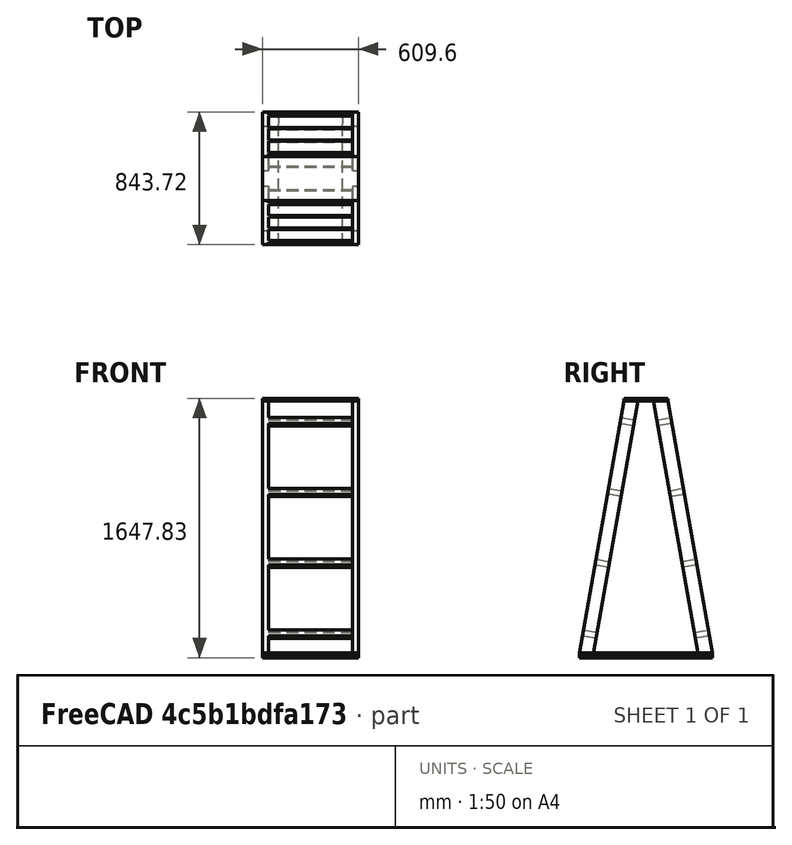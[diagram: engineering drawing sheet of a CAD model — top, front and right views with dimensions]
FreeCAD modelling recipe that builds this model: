
FCSTD DOCUMENT  (FreeCAD 0.20R29410 (Git))
Label: ClampRack
License: All rights reserved
LicenseURL: http://en.wikipedia.org/wiki/All_rights_reserved
objects: TechDraw::DrawViewDimension×22, Sketcher::SketchObject×13, PartDesign::Pad×12, Part::Part2DObjectPython×10, PartDesign::Body×10, TechDraw::DrawViewPart×6, TechDraw::DrawProjGroupItem×6, TechDraw::DrawSVGTemplate×3, TechDraw::DrawProjGroup×3, TechDraw::DrawPage×3, PartDesign::Plane×2, Spreadsheet::Sheet×1, App::LinkGroup×1
note: 59 computed .brp shape members not serialized (recipe doc carries the construction recipe); baked Part::Feature solids carry a one-line shape summary decoded from their .brp

FEATURE [Sketcher::SketchObject] Sketch  label="YZ_profile"
  FullyConstrained = true
  MapMode = 5
  Placement = pos=(0,0,0) rot=(0.57735,0.57735,0.57735;2.0944rad)
  Support = -> [YZ_Plane]
  expr: Constraints[14] = <<Spreadsheet>>.riser_z
  expr: Constraints[23] = <<Spreadsheet>>.shelf_stock_height
  expr: Constraints[35] = <<Spreadsheet>>.top_shelf_y
  expr: Constraints[50] = <<Spreadsheet>>.shelf_stock_height
  expr: Constraints[77] = <<Spreadsheet>>.riser_stock_width
  expr: Constraints[9] = <<Spreadsheet>>.shelf_stock_height
  sketch-geometry (29):
    g0: LineSegment StartX=-421.858 StartY=0 StartZ=0 EndX=421.858 EndY=0 EndZ=0
    g1: LineSegment StartX=421.858 StartY=0 StartZ=0 EndX=421.858 EndY=-15.875 EndZ=0
    g2: LineSegment StartX=421.858 StartY=-15.875 StartZ=0 EndX=-421.858 EndY=-15.875 EndZ=0
    g3: LineSegment StartX=-421.858 StartY=-15.875 StartZ=0 EndX=-421.858 EndY=0 EndZ=0
    g4: LineSegment StartX=-331.587 StartY=0 StartZ=0 EndX=-49.4286 EndY=1600.2 EndZ=0
    g5: LineSegment StartX=-49.4286 StartY=1600.2 StartZ=0 EndX=-139.7 EndY=1600.2 EndZ=0
    g6: LineSegment StartX=-139.7 StartY=1600.2 StartZ=0 EndX=139.7 EndY=1600.2 EndZ=0
    g7: LineSegment StartX=139.7 StartY=1600.2 StartZ=0 EndX=139.7 EndY=1616.08 EndZ=0
    g8: LineSegment StartX=139.7 StartY=1616.08 StartZ=0 EndX=-139.7 EndY=1616.08 EndZ=0
    g9: LineSegment StartX=-139.7 StartY=1616.08 StartZ=0 EndX=-139.7 EndY=1600.2 EndZ=0
    g10: LineSegment StartX=139.7 StartY=1600.2 StartZ=0 EndX=49.4286 EndY=1600.2 EndZ=0
    g11: LineSegment StartX=49.4286 StartY=1600.2 StartZ=0 EndX=331.587 EndY=0 EndZ=0
    g12: LineSegment StartX=331.587 StartY=0 StartZ=0 EndX=421.858 EndY=0 EndZ=0
    g13: LineSegment StartX=-139.7 StartY=1600.2 StartZ=0 EndX=-161.753 EndY=1475.13 EndZ=0
    g14: LineSegment StartX=-399.805 StartY=125.071 StartZ=0 EndX=-421.858 EndY=0 EndZ=0
    g15: LineSegment StartX=-421.858 StartY=-15.875 StartZ=0 EndX=421.858 EndY=-15.875 EndZ=0
    g16: LineSegment StartX=421.858 StartY=-15.875 StartZ=0 EndX=421.858 EndY=-31.75 EndZ=0
    g17: LineSegment StartX=421.858 StartY=-31.75 StartZ=0 EndX=-421.858 EndY=-31.75 EndZ=0
    g18: LineSegment StartX=-421.858 StartY=-31.75 StartZ=0 EndX=-421.858 EndY=-15.875 EndZ=0
    g19: LineSegment StartX=-161.753 StartY=1475.13 StartZ=0 EndX=-241.104 EndY=1025.11 EndZ=0
    g20: LineSegment StartX=-241.104 StartY=1025.11 StartZ=0 EndX=-320.455 EndY=575.09 EndZ=0
    g21: LineSegment StartX=-320.455 StartY=575.09 StartZ=0 EndX=-399.805 EndY=125.071 EndZ=0
    g22: LineSegment StartX=161.753 StartY=1475.13 StartZ=0 EndX=139.7 EndY=1600.2 EndZ=0
    g23: LineSegment StartX=421.858 StartY=0 StartZ=0 EndX=399.805 EndY=125.071 EndZ=0
    g24: LineSegment StartX=241.104 StartY=1025.11 StartZ=0 EndX=161.753 EndY=1475.13 EndZ=0
    g25: LineSegment StartX=399.805 StartY=125.071 StartZ=0 EndX=320.455 EndY=575.09 EndZ=0
    g26: LineSegment StartX=320.455 StartY=575.09 StartZ=0 EndX=241.104 EndY=1025.11 EndZ=0
    g27: LineSegment StartX=-161.753 StartY=1475.13 StartZ=0 EndX=-74.2039 EndY=1459.69 EndZ=0
    g28: LineSegment StartX=161.753 StartY=1475.13 StartZ=0 EndX=74.2039 EndY=1459.69 EndZ=0
  constraints (78):
    c: Coincident(g0,g1)
    c: Coincident(g1,g2)
    c: Coincident(g2,g3)
    c: Coincident(g3,g0)
    c: Horizontal(g0)
    c: Horizontal(g2)
    c: Vertical(g1)
    c: Vertical(g3)
    c: Symmetric(g0,g0,g-1)
    c: DistanceY(g3,g3) = 15.875
    c: PointOnObject(g4,g0)
    c: Horizontal(g5)
    c: Coincident(g5,g13)
    c: Coincident(g14,g0)
    c: DistanceY(g4,g4) = 1600.2
    c: Angle(g4,g-2) = 0.174533
    c: Coincident(g6,g7)
    c: Coincident(g7,g8)
    c: Coincident(g8,g9)
    c: Coincident(g9,g6)
    c: Horizontal(g6)
    c: Vertical(g7)
    c: Vertical(g9)
    c: DistanceY(g6,g8) = 15.875
    c: Coincident(g6,g5)
    c: Symmetric(g8,g7,g-2)
    c: Coincident(g5,g4)
    c: Coincident(g0,g23)
    c: Coincident(g22,g6)
    c: Coincident(g22,g10)
    c: PointOnObject(g10,g6)
    c: Coincident(g10,g11)
    c: PointOnObject(g11,g0)
    c: Coincident(g11,g12)
    c: Coincident(g12,g23)
    c: DistanceX(g8,g8) = 279.4
    c: Coincident(g13,g19)
    c: Parallel(g4,g13)
    c: Coincident(g21,g14)
    c: Parallel(g4,g14)
    c: Distance(g13) = 127
    c: Coincident(g15,g16)
    c: Coincident(g16,g17)
    c: Coincident(g17,g18)
    c: Coincident(g18,g15)
    c: Horizontal(g17)
    c: Vertical(g16)
    c: Vertical(g18)
    c: Coincident(g15,g2)
    c: Coincident(g1,g15)
    c: DistanceY(g18,g18) = 15.875
    c: Coincident(g19,g20)
    c: Parallel(g4,g19)
    c: Coincident(g20,g21)
    c: Parallel(g4,g20)
    c: Parallel(g4,g21)
    c: Equal(g21,g20)
    c: Equal(g20,g19)
    c: Coincident(g24,g22)
    c: Parallel(g11,g22)
    c: Coincident(g23,g25)
    c: Coincident(g26,g24)
    c: Parallel(g11,g24)
    c: Coincident(g25,g26)
    c: Parallel(g11,g25)
    c: Equal(g25,g26)
    c: Equal(g26,g24)
    c: Coincident(g27,g13)
    c: PointOnObject(g27,g4)
    c: Coincident(g28,g22)
    c: PointOnObject(g28,g11)
    c: Perpendicular(g27,g13)
    c: Perpendicular(g28,g22)
    c: Symmetric(g13,g22,g-2)
    c: Symmetric(g14,g23,g-2)
    c: Distance(g14,g0) = 127
    c: Distance(g27) = 88.9
    c: Distance(g28) = 88.9
FEATURE [Part::Part2DObjectPython] Clone2D  label="YZ_profile (2D)"  # Draft 2D object (typed FeaturePython)
  Fuse = false
  Objects = -> [Sketch]
  Placement = pos=(0,0,0) rot=(0.57735,0.57735,0.57735;2.0944rad)
  Scale = (1,1,1)
FEATURE [Sketcher::SketchObject] Sketch001
  ExternalGeometry = -> [Clone2D]
  FullyConstrained = true
  MapMode = 5
  Placement = pos=(0,0,0) rot=(0.57735,0.57735,0.57735;2.0944rad)
  Support = -> [YZ_Plane]
  sketch-geometry (4):
    g0: LineSegment StartX=-421.858 StartY=-2.13e-14 StartZ=0 EndX=421.858 EndY=-2.13e-14 EndZ=0
    g1: LineSegment StartX=421.858 StartY=-2.13e-14 StartZ=0 EndX=421.858 EndY=-15.875 EndZ=0
    g2: LineSegment StartX=421.858 StartY=-15.875 StartZ=0 EndX=-421.858 EndY=-15.875 EndZ=0
    g3: LineSegment StartX=-421.858 StartY=-15.875 StartZ=0 EndX=-421.858 EndY=-2.13e-14 EndZ=0
  constraints (9):
    c: Coincident(g0,g1)
    c: Coincident(g1,g2)
    c: Coincident(g2,g3)
    c: Coincident(g3,g0)
    c: Horizontal(g2)
    c: Vertical(g1)
    c: Coincident(g0,g-4)
    c: Coincident(g-5,g2)
    c: Coincident(g0,g-6)
FEATURE [PartDesign::Pad] Pad
  Direction = (1,-2e-16,3e-16)
  Length = 609.6
  Length2 = 10
  Midplane = true
  Placement = pos=(0,0,0) rot=(0.57735,0.57735,0.57735;2.0944rad)
  Profile = -> Sketch001
  ReferenceAxis = -> Sketch001 [N_Axis]
  Refine = true
  Type = 0
  expr: Length = Spreadsheet.width_x
FEATURE [PartDesign::Body] Body  label="BottomShelf"
  Group = -> [Clone2D,Sketch001,Pad]
  Origin = -> Origin
  Tip = -> Pad
FEATURE [Part::Part2DObjectPython] Clone2D001  label="YZ_profile (2D)001"  # Draft 2D object (typed FeaturePython)
  Fuse = false
  Objects = -> [Sketch]
  Placement = pos=(0,0,0) rot=(0.57735,0.57735,0.57735;2.0944rad)
  Scale = (1,1,1)
FEATURE [Sketcher::SketchObject] Sketch005
  ExternalGeometry = -> [Clone2D001]
  FullyConstrained = true
  MapMode = 5
  Placement = pos=(0,0,0) rot=(0.57735,0.57735,0.57735;2.0944rad)
  Support = -> [YZ_Plane004]
  sketch-geometry (4):
    g0: LineSegment StartX=-421.858 StartY=-2.84e-14 StartZ=0 EndX=-139.7 EndY=1600.2 EndZ=0
    g1: LineSegment StartX=-139.7 StartY=1600.2 StartZ=0 EndX=-49.4286 EndY=1600.2 EndZ=0
    g2: LineSegment StartX=-49.4286 StartY=1600.2 StartZ=0 EndX=-331.587 EndY=0 EndZ=0
    g3: LineSegment StartX=-331.587 StartY=0 StartZ=0 EndX=-421.858 EndY=-2.84e-14 EndZ=0
  constraints (8):
    c: Coincident(g0,g1)
    c: Coincident(g1,g2)
    c: Coincident(g2,g3)
    c: Coincident(g3,g0)
    c: Coincident(g0,g-3)
    c: Coincident(g1,g-4)
    c: Coincident(g0,g-5)
    c: Coincident(g2,g-6)
FEATURE [PartDesign::Pad] Pad003
  Direction = (1,-2e-16,3e-16)
  Length = 38.1
  Length2 = 10
  Midplane = true
  Placement = pos=(0,0,0) rot=(0.57735,0.57735,0.57735;2.0944rad)
  Profile = -> Sketch005
  ReferenceAxis = -> Sketch005 [N_Axis]
  Refine = true
  Type = 0
FEATURE [PartDesign::Body] Body003  label="RiserFtRt"
  Group = -> [Clone2D001,Sketch005,Pad003]
  Origin = -> Origin003
  Placement = pos=(285.75,0,0) rot=(0,0,1;0rad)
  Tip = -> Pad003
FEATURE [Part::Part2DObjectPython] Clone2D002  label="YZ_profile (2D)002"  # Draft 2D object (typed FeaturePython)
  Fuse = false
  Objects = -> [Sketch]
  Placement = pos=(0,0,0) rot=(0.57735,0.57735,0.57735;2.0944rad)
  Scale = (1,1,1)
FEATURE [Sketcher::SketchObject] Sketch006
  ExternalGeometry = -> [Clone2D002]
  FullyConstrained = true
  MapMode = 5
  Placement = pos=(0,0,0) rot=(0.57735,0.57735,0.57735;2.0944rad)
  Support = -> [YZ_Plane004]
  sketch-geometry (4):
    g0: LineSegment StartX=-421.858 StartY=-2.84e-14 StartZ=0 EndX=-139.7 EndY=1600.2 EndZ=0
    g1: LineSegment StartX=-139.7 StartY=1600.2 StartZ=0 EndX=-49.4286 EndY=1600.2 EndZ=0
    g2: LineSegment StartX=-49.4286 StartY=1600.2 StartZ=0 EndX=-331.587 EndY=0 EndZ=0
    g3: LineSegment StartX=-331.587 StartY=0 StartZ=0 EndX=-421.858 EndY=-2.84e-14 EndZ=0
  constraints (8):
    c: Coincident(g0,g1)
    c: Coincident(g1,g2)
    c: Coincident(g2,g3)
    c: Coincident(g3,g0)
    c: Coincident(g0,g-3)
    c: Coincident(g1,g-4)
    c: Coincident(g0,g-5)
    c: Coincident(g2,g-6)
FEATURE [PartDesign::Pad] Pad004
  Direction = (1,-2e-16,3e-16)
  Length = 38.1
  Length2 = 10
  Midplane = true
  Placement = pos=(0,0,0) rot=(0.57735,0.57735,0.57735;2.0944rad)
  Profile = -> Sketch006
  ReferenceAxis = -> Sketch006 [N_Axis]
  Refine = true
  Type = 0
FEATURE [Part::Part2DObjectPython] Clone2D003  label="YZ_profile (2D)003"  # Draft 2D object (typed FeaturePython)
  Fuse = false
  Objects = -> [Sketch]
  Placement = pos=(0,0,0) rot=(0.57735,0.57735,0.57735;2.0944rad)
  Scale = (1,1,1)
FEATURE [Sketcher::SketchObject] Sketch007
  ExternalGeometry = -> [Clone2D003]
  FullyConstrained = true
  MapMode = 5
  Placement = pos=(0,0,0) rot=(0.57735,0.57735,0.57735;2.0944rad)
  Support = -> [YZ_Plane005]
  sketch-geometry (4):
    g0: LineSegment StartX=49.4286 StartY=1600.2 StartZ=0 EndX=139.7 EndY=1600.2 EndZ=0
    g1: LineSegment StartX=139.7 StartY=1600.2 StartZ=0 EndX=421.858 EndY=0 EndZ=0
    g2: LineSegment StartX=421.858 StartY=0 StartZ=0 EndX=331.587 EndY=2.13e-14 EndZ=0
    g3: LineSegment StartX=331.587 StartY=2.13e-14 StartZ=0 EndX=49.4286 EndY=1600.2 EndZ=0
  constraints (8):
    c: Coincident(g0,g1)
    c: Coincident(g1,g2)
    c: Coincident(g2,g3)
    c: Coincident(g3,g0)
    c: Coincident(g0,g-4)
    c: Coincident(g1,g-6)
    c: Coincident(g2,g-5)
    c: Coincident(g-3,g0)
FEATURE [PartDesign::Pad] Pad005
  Direction = (1,-2e-16,3e-16)
  Length = 38.1
  Length2 = 10
  Placement = pos=(0,0,0) rot=(0.57735,0.57735,0.57735;2.0944rad)
  Profile = -> Sketch007
  ReferenceAxis = -> Sketch007 [N_Axis]
  Refine = true
  Type = 0
FEATURE [PartDesign::Body] Body005  label="RiserRrRt"
  Group = -> [Clone2D003,Sketch007,Pad005]
  Origin = -> Origin005
  Placement = pos=(266.7,0,0) rot=(0,0,1;0rad)
  Tip = -> Pad005
FEATURE [Part::Part2DObjectPython] Clone2D004  label="YZ_profile (2D)004"  # Draft 2D object (typed FeaturePython)
  Fuse = false
  Objects = -> [Sketch]
  Placement = pos=(0,0,0) rot=(0.57735,0.57735,0.57735;2.0944rad)
  Scale = (1,1,1)
FEATURE [Sketcher::SketchObject] Sketch008
  ExternalGeometry = -> [Clone2D004]
  FullyConstrained = true
  MapMode = 5
  Placement = pos=(0,0,0) rot=(0.57735,0.57735,0.57735;2.0944rad)
  Support = -> [YZ_Plane005]
  sketch-geometry (4):
    g0: LineSegment StartX=49.4286 StartY=1600.2 StartZ=0 EndX=139.7 EndY=1600.2 EndZ=0
    g1: LineSegment StartX=139.7 StartY=1600.2 StartZ=0 EndX=421.858 EndY=0 EndZ=0
    g2: LineSegment StartX=421.858 StartY=0 StartZ=0 EndX=331.587 EndY=2.13e-14 EndZ=0
    g3: LineSegment StartX=331.587 StartY=2.13e-14 StartZ=0 EndX=49.4286 EndY=1600.2 EndZ=0
  constraints (8):
    c: Coincident(g0,g1)
    c: Coincident(g1,g2)
    c: Coincident(g2,g3)
    c: Coincident(g3,g0)
    c: Coincident(g0,g-4)
    c: Coincident(g1,g-6)
    c: Coincident(g2,g-5)
    c: Coincident(g-3,g0)
FEATURE [PartDesign::Pad] Pad006
  Direction = (1,-2e-16,3e-16)
  Length = 38.1
  Length2 = 10
  Placement = pos=(0,0,0) rot=(0.57735,0.57735,0.57735;2.0944rad)
  Profile = -> Sketch008
  ReferenceAxis = -> Sketch008 [N_Axis]
  Refine = true
  Type = 0
FEATURE [Part::Part2DObjectPython] Clone2D005  label="YZ_profile (2D)005"  # Draft 2D object (typed FeaturePython)
  Fuse = false
  Objects = -> [Sketch]
  Placement = pos=(0,0,0) rot=(0.57735,0.57735,0.57735;2.0944rad)
  Scale = (1,1,1)
FEATURE [Sketcher::SketchObject] Sketch009
  ExternalGeometry = -> [Clone2D005]
  FullyConstrained = true
  MapMode = 5
  Placement = pos=(0,0,0) rot=(0.57735,0.57735,0.57735;2.0944rad)
  Support = -> [YZ_Plane006]
  sketch-geometry (4):
    g0: LineSegment StartX=-139.7 StartY=1616.08 StartZ=0 EndX=139.7 EndY=1616.08 EndZ=0
    g1: LineSegment StartX=139.7 StartY=1616.08 StartZ=0 EndX=139.7 EndY=1600.2 EndZ=0
    g2: LineSegment StartX=139.7 StartY=1600.2 StartZ=0 EndX=-139.7 EndY=1600.2 EndZ=0
    g3: LineSegment StartX=-139.7 StartY=1600.2 StartZ=0 EndX=-139.7 EndY=1616.08 EndZ=0
  constraints (8):
    c: Coincident(g0,g1)
    c: Coincident(g1,g2)
    c: Coincident(g2,g3)
    c: Coincident(g3,g0)
    c: Coincident(g0,g-3)
    c: Coincident(g2,g-4)
    c: Coincident(g1,g-5)
    c: Coincident(g0,g-6)
FEATURE [PartDesign::Pad] Pad007
  Direction = (1,-2e-16,3e-16)
  Length = 609.6
  Length2 = 10
  Midplane = true
  Placement = pos=(0,0,0) rot=(0.57735,0.57735,0.57735;2.0944rad)
  Profile = -> Sketch009
  ReferenceAxis = -> Sketch009 [N_Axis]
  Refine = true
  Type = 0
  expr: Length = Spreadsheet.width_x
FEATURE [PartDesign::Body] Body007  label="TopShelf"
  Group = -> [Clone2D005,Sketch009,Pad007]
  Origin = -> Origin007
  Tip = -> Pad007
FEATURE [Spreadsheet::Sheet] Spreadsheet
  cells = A2=riser_stock_width; B2(riser_stock_width)==3.5"; C2==3.5"; A3=riser_stock_height; B3(riser_stock_height)==1.5"; C3==1.5"; A4=stretcher_stock_width; B4(stretcher_stock_width)==3.5"; C4==3.5"; A5=stretcher_stock_height; B5(stretcher_stock_height)==1.5"; C5==1.5"; A6=shelf_stock_height; B6(shelf_stock_height)==1" * 5 / 8; C6==1" * 5 / 8; A7=width; B7(width_x)==24"; C7==24"; A8=riser_z; B8(riser_z)==5' + 3"; C8==5' + 3"; A9=top_shelf_y; B9(top_shelf_y)==11"; C9==11"; A10=stretcher_x; B10(stretcher_x)==width_x - 2 * riser_stock_height; C10==width_x - 2 * riser_stock_height; A11=base_rail_width; B11(base_rail_width)==4"; C11==4"; A12=base_stock_height; B12(base_stock_height)==1" * 5 / 8; C12==1" * 5 / 8
FEATURE [PartDesign::Plane] DatumPlane
  Length = 60
  MapMode = 5
  Placement = pos=(19.05,-8.5e-15,6.3e-15) rot=(0.57735,0.57735,0.57735;2.0944rad)
  ResizeMode = 0
  Support = -> [Pad004]
  Width = 60
FEATURE [Sketcher::SketchObject] Sketch010
  ExternalGeometry = -> [Clone2D002]
  FullyConstrained = true
  MapMode = 5
  Placement = pos=(19.05,-8.5e-15,6.3e-15) rot=(0.57735,0.57735,0.57735;2.0944rad)
  Support = -> [DatumPlane]
  expr: Constraints[35] = <<Spreadsheet>>.stretcher_stock_width
  expr: Constraints[36] = <<Spreadsheet>>.stretcher_stock_height
  sketch-geometry (16):
    g0: LineSegment StartX=-237.796 StartY=1043.87 StartZ=0 EndX=-150.247 EndY=1028.43 EndZ=0
    g1: LineSegment StartX=-150.247 StartY=1028.43 StartZ=0 EndX=-156.863 EndY=990.912 EndZ=0
    g2: LineSegment StartX=-156.863 StartY=990.912 StartZ=0 EndX=-244.412 EndY=1006.35 EndZ=0
    g3: LineSegment StartX=-244.412 StartY=1006.35 StartZ=0 EndX=-237.796 EndY=1043.87 EndZ=0
    g4: LineSegment StartX=-317.147 StartY=593.851 StartZ=0 EndX=-229.597 EndY=578.413 EndZ=0
    g5: LineSegment StartX=-229.597 StartY=578.413 StartZ=0 EndX=-236.213 EndY=540.892 EndZ=0
    g6: LineSegment StartX=-236.213 StartY=540.892 StartZ=0 EndX=-323.763 EndY=556.33 EndZ=0
    g7: LineSegment StartX=-323.763 StartY=556.33 StartZ=0 EndX=-317.147 EndY=593.851 EndZ=0
    g8: LineSegment StartX=-396.497 StartY=143.831 StartZ=0 EndX=-308.948 EndY=128.394 EndZ=0
    g9: LineSegment StartX=-308.948 StartY=128.394 StartZ=0 EndX=-315.564 EndY=90.8727 EndZ=0
    g10: LineSegment StartX=-315.564 StartY=90.8727 StartZ=0 EndX=-403.113 EndY=106.31 EndZ=0
    g11: LineSegment StartX=-403.113 StartY=106.31 StartZ=0 EndX=-396.497 EndY=143.831 EndZ=0
    g12: LineSegment StartX=-158.445 StartY=1493.89 StartZ=0 EndX=-70.8959 EndY=1478.45 EndZ=0
    g13: LineSegment StartX=-70.8959 StartY=1478.45 StartZ=0 EndX=-77.5119 EndY=1440.93 EndZ=0
    g14: LineSegment StartX=-77.5119 StartY=1440.93 StartZ=0 EndX=-165.061 EndY=1456.37 EndZ=0
    g15: LineSegment StartX=-165.061 StartY=1456.37 StartZ=0 EndX=-158.445 EndY=1493.89 EndZ=0
  constraints (44):
    c: Coincident(g0,g1)
    c: Coincident(g1,g2)
    c: Coincident(g2,g3)
    c: Coincident(g3,g0)
    c: Coincident(g4,g5)
    c: Coincident(g5,g6)
    c: Coincident(g6,g7)
    c: Coincident(g7,g4)
    c: Coincident(g8,g9)
    c: Coincident(g9,g10)
    c: Coincident(g10,g11)
    c: Coincident(g11,g8)
    c: Parallel(g0,g2)
    c: Parallel(g2,g4)
    c: Parallel(g4,g6)
    c: Parallel(g6,g8)
    c: Parallel(g8,g10)
    c: Parallel(g3,g1)
    c: Parallel(g1,g7)
    c: Parallel(g5,g11)
    c: Parallel(g11,g9)
    c: Equal(g3,g7)
    c: Equal(g7,g11)
    c: Equal(g4,g8)
    c: Symmetric(g8,g10,g-7)
    c: Symmetric(g4,g6,g-6)
    c: Symmetric(g2,g0,g-5)
    c: Coincident(g12,g13)
    c: Coincident(g13,g14)
    c: Coincident(g14,g15)
    c: Coincident(g15,g12)
    c: Parallel(g15,g13)
    c: PointOnObject(g12,g-3)
    c: Symmetric(g14,g12,g-4)
    c: Perpendicular(g13,g12)
    c: Distance(g12) = 88.9
    c: Distance(g13) = 38.1
    c: Equal(g12,g0)
    c: Equal(g0,g4)
    c: Equal(g10,g6)
    c: Parallel(g6,g12)
    c: Parallel(g12,g14)
    c: Equal(g13,g1)
    c: PointOnObject(g0,g-4)
FEATURE [PartDesign::Plane] DatumPlane001
  Length = 60
  MapMode = 5
  Placement = pos=(38.1,-1.69e-14,1.27e-14) rot=(0.57735,0.57735,0.57735;2.0944rad)
  ResizeMode = 0
  Support = -> [Pad006]
  Width = 60
FEATURE [Sketcher::SketchObject] Sketch011
  ExternalGeometry = -> [Clone2D004]
  FullyConstrained = true
  MapMode = 5
  Placement = pos=(38.1,-1.69e-14,1.27e-14) rot=(0.57735,0.57735,0.57735;2.0944rad)
  Support = -> [DatumPlane001]
  expr: Constraints[32] = <<Spreadsheet>>.stretcher_stock_width
  expr: Constraints[40] = <<Spreadsheet>>.stretcher_stock_height
  sketch-geometry (16):
    g0: LineSegment StartX=70.8959 StartY=1478.45 StartZ=0 EndX=158.445 EndY=1493.89 EndZ=0
    g1: LineSegment StartX=158.445 StartY=1493.89 StartZ=0 EndX=165.061 EndY=1456.37 EndZ=0
    g2: LineSegment StartX=165.061 StartY=1456.37 StartZ=0 EndX=77.5119 EndY=1440.93 EndZ=0
    g3: LineSegment StartX=77.5119 StartY=1440.93 StartZ=0 EndX=70.8959 EndY=1478.45 EndZ=0
    g4: LineSegment StartX=150.247 StartY=1028.43 StartZ=0 EndX=237.796 EndY=1043.87 EndZ=0
    g5: LineSegment StartX=237.796 StartY=1043.87 StartZ=0 EndX=244.412 EndY=1006.35 EndZ=0
    g6: LineSegment StartX=244.412 StartY=1006.35 StartZ=0 EndX=156.863 EndY=990.912 EndZ=0
    g7: LineSegment StartX=156.863 StartY=990.912 StartZ=0 EndX=150.247 EndY=1028.43 EndZ=0
    g8: LineSegment StartX=229.597 StartY=578.413 StartZ=0 EndX=317.147 EndY=593.851 EndZ=0
    g9: LineSegment StartX=317.147 StartY=593.851 StartZ=0 EndX=323.763 EndY=556.33 EndZ=0
    g10: LineSegment StartX=323.763 StartY=556.33 StartZ=0 EndX=236.213 EndY=540.892 EndZ=0
    g11: LineSegment StartX=236.213 StartY=540.892 StartZ=0 EndX=229.597 EndY=578.413 EndZ=0
    g12: LineSegment StartX=308.948 StartY=128.394 StartZ=0 EndX=396.497 EndY=143.831 EndZ=0
    g13: LineSegment StartX=396.497 StartY=143.831 StartZ=0 EndX=403.113 EndY=106.31 EndZ=0
    g14: LineSegment StartX=403.113 StartY=106.31 StartZ=0 EndX=315.564 EndY=90.8727 EndZ=0
    g15: LineSegment StartX=315.564 StartY=90.8727 StartZ=0 EndX=308.948 EndY=128.394 EndZ=0
  constraints (44):
    c: Coincident(g0,g1)
    c: Coincident(g1,g2)
    c: Coincident(g2,g3)
    c: Coincident(g3,g0)
    c: Coincident(g4,g5)
    c: Coincident(g5,g6)
    c: Coincident(g6,g7)
    c: Coincident(g7,g4)
    c: Coincident(g8,g9)
    c: Coincident(g9,g10)
    c: Coincident(g10,g11)
    c: Coincident(g11,g8)
    c: Coincident(g12,g13)
    c: Coincident(g13,g14)
    c: Coincident(g14,g15)
    c: Coincident(g15,g12)
    c: PointOnObject(g12,g-6)
    c: PointOnObject(g8,g-5)
    c: PointOnObject(g4,g-4)
    c: PointOnObject(g1,g-4)
    c: Parallel(g3,g1)
    c: Parallel(g7,g5)
    c: Parallel(g11,g9)
    c: Parallel(g15,g13)
    c: Parallel(g14,g12)
    c: Parallel(g10,g8)
    c: Parallel(g6,g4)
    c: Parallel(g2,g0)
    c: Symmetric(g0,g1,g-4)
    c: Symmetric(g4,g5,g-5)
    c: Symmetric(g8,g9,g-6)
    c: Symmetric(g12,g13,g-7)
    c: Distance(g0) = 88.9
    c: Equal(g2,g4)
    c: Equal(g6,g8)
    c: Equal(g10,g12)
    c: Perpendicular(g1,g0)
    c: Perpendicular(g5,g4)
    c: Perpendicular(g9,g8)
    c: Perpendicular(g13,g12)
    c: Distance(g3) = 38.1
    c: Equal(g3,g7)
    c: Equal(g11,g3)
    c: Equal(g15,g3)
FEATURE [PartDesign::Pad] Pad009
  BaseFeature = -> Pad006
  Direction = (1,-4e-16,2e-16)
  Length = 533.4
  Length2 = 10
  Placement = pos=(0,0,0) rot=(0.57735,0.57735,0.57735;2.0944rad)
  Profile = -> Sketch011
  ReferenceAxis = -> Sketch011 [N_Axis]
  Refine = true
  Type = 0
  expr: Length = <<Spreadsheet>>.stretcher_x
FEATURE [PartDesign::Body] Body006  label="RiserRrLf"
  Group = -> [Clone2D004,Sketch008,Pad006,DatumPlane001,Sketch011,Pad009]
  Origin = -> Origin006
  Placement = pos=(-304.8,0,0) rot=(0,0,1;0rad)
  Tip = -> Pad009
FEATURE [PartDesign::Pad] Pad010
  BaseFeature = -> Pad004
  Direction = (1,-4e-16,2e-16)
  Length = 533.4
  Length2 = 10
  Placement = pos=(0,0,0) rot=(0.57735,0.57735,0.57735;2.0944rad)
  Profile = -> Sketch010
  ReferenceAxis = -> Sketch010 [N_Axis]
  Refine = true
  Type = 0
  expr: Length = <<Spreadsheet>>.stretcher_x
FEATURE [PartDesign::Body] Body004  label="RiserFtLf"
  Group = -> [Sketch006,Pad004,DatumPlane,Sketch010,Clone2D002,Pad010]
  Origin = -> Origin004
  Placement = pos=(-285.75,0,0) rot=(0,0,1;0rad)
  Tip = -> Pad010
FEATURE [Part::Part2DObjectPython] Clone2D006  label="YZ_profile (2D)006"  # Draft 2D object (typed FeaturePython)
  Fuse = false
  Objects = -> [Sketch]
  Placement = pos=(0,0,0) rot=(0.57735,0.57735,0.57735;2.0944rad)
  Scale = (1,1,1)
FEATURE [Part::Part2DObjectPython] Clone2D007  label="YZ_profile (2D)007"  # Draft 2D object (typed FeaturePython)
  Fuse = false
  Objects = -> [Sketch]
  Placement = pos=(0,0,0) rot=(0.57735,0.57735,0.57735;2.0944rad)
  Scale = (1,1,1)
FEATURE [Sketcher::SketchObject] Sketch013
  ExternalGeometry = -> [Clone2D007]
  FullyConstrained = true
  MapMode = 5
  Placement = pos=(0,0,0) rot=(0.57735,0.57735,0.57735;2.0944rad)
  Support = -> [YZ_Plane003]
  sketch-geometry (4):
    g0: LineSegment StartX=-421.858 StartY=-15.875 StartZ=0 EndX=421.858 EndY=-15.875 EndZ=0
    g1: LineSegment StartX=421.858 StartY=-15.875 StartZ=0 EndX=421.858 EndY=-31.75 EndZ=0
    g2: LineSegment StartX=421.858 StartY=-31.75 StartZ=0 EndX=-421.858 EndY=-31.75 EndZ=0
    g3: LineSegment StartX=-421.858 StartY=-31.75 StartZ=0 EndX=-421.858 EndY=-15.875 EndZ=0
  constraints (8):
    c: Coincident(g0,g1)
    c: Coincident(g1,g2)
    c: Coincident(g2,g3)
    c: Coincident(g3,g0)
    c: Coincident(g0,g-3)
    c: Coincident(g-4,g2)
    c: Coincident(g1,g-6)
    c: Coincident(g0,g-5)
FEATURE [Sketcher::SketchObject] Sketch014
  ExternalGeometry = -> [Clone2D006]
  FullyConstrained = true
  MapMode = 5
  Placement = pos=(0,0,0) rot=(0.57735,0.57735,0.57735;2.0944rad)
  Support = -> [YZ_Plane001]
  sketch-geometry (4):
    g0: LineSegment StartX=-421.858 StartY=-15.875 StartZ=0 EndX=421.858 EndY=-15.875 EndZ=0
    g1: LineSegment StartX=421.858 StartY=-15.875 StartZ=0 EndX=421.858 EndY=-31.75 EndZ=0
    g2: LineSegment StartX=421.858 StartY=-31.75 StartZ=0 EndX=-421.858 EndY=-31.75 EndZ=0
    g3: LineSegment StartX=-421.858 StartY=-31.75 StartZ=0 EndX=-421.858 EndY=-15.875 EndZ=0
  constraints (8):
    c: Coincident(g0,g1)
    c: Coincident(g1,g2)
    c: Coincident(g2,g3)
    c: Coincident(g3,g0)
    c: Coincident(g0,g-3)
    c: Coincident(g2,g-4)
    c: Coincident(g1,g-6)
    c: Coincident(g0,g-5)
FEATURE [PartDesign::Pad] Pad011
  Direction = (1,-2e-16,3e-16)
  Length = 101.6
  Length2 = 10
  Midplane = true
  Placement = pos=(0,0,0) rot=(0.57735,0.57735,0.57735;2.0944rad)
  Profile = -> Sketch014
  ReferenceAxis = -> Sketch014 [N_Axis]
  Refine = true
  Type = 0
  expr: Length = <<Spreadsheet>>.base_rail_width
FEATURE [PartDesign::Body] Body001  label="LowerBraceRt"
  Group = -> [Clone2D006,Sketch014,Pad011]
  Origin = -> Origin001
  Placement = pos=(254,0,0) rot=(0,0,1;0rad)
  Tip = -> Pad011
  expr: .Placement.Base.x = (<<Spreadsheet>>.width_x - <<Spreadsheet>>.base_rail_width) / 2
FEATURE [PartDesign::Pad] Pad012
  Direction = (1,-2e-16,3e-16)
  Length = 101.6
  Length2 = 10
  Midplane = true
  Placement = pos=(0,0,0) rot=(0.57735,0.57735,0.57735;2.0944rad)
  Profile = -> Sketch013
  ReferenceAxis = -> Sketch013 [N_Axis]
  Refine = true
  Type = 0
  expr: Length = <<Spreadsheet>>.base_rail_width
FEATURE [PartDesign::Body] Body002  label="LowerBraceLf"
  Group = -> [Clone2D007,Sketch013,Pad012]
  Origin = -> Origin002
  Placement = pos=(-254,0,0) rot=(0,0,1;0rad)
  Tip = -> Pad012
  expr: .Placement.Base.x = (<<Spreadsheet>>.width_x - <<Spreadsheet>>.base_rail_width) / 2 * -1
FEATURE [Part::Part2DObjectPython] Clone2D008  label="YZ_profile (2D)008"  # Draft 2D object (typed FeaturePython)
  Fuse = false
  Objects = -> [Sketch]
  Placement = pos=(0,0,0) rot=(0.57735,0.57735,0.57735;2.0944rad)
  Scale = (1,1,1)
FEATURE [Part::Part2DObjectPython] Clone2D009  label="YZ_profile (2D)009"  # Draft 2D object (typed FeaturePython)
  Fuse = false
  Objects = -> [Sketch]
  Placement = pos=(0,0,0) rot=(0.57735,0.57735,0.57735;2.0944rad)
  Scale = (1,1,1)
FEATURE [Sketcher::SketchObject] Sketch015
  ExternalGeometry = -> [Clone2D008]
  FullyConstrained = true
  MapMode = 5
  Placement = pos=(0,0,0) rot=(0.57735,0.57735,0.57735;2.0944rad)
  Support = -> [YZ_Plane007]
  expr: Constraints[10] = <<Spreadsheet>>.base_rail_width
  expr: Constraints[9] = Spreadsheet.base_stock_height
  sketch-geometry (4):
    g0: LineSegment StartX=-421.858 StartY=-15.875 StartZ=0 EndX=-320.258 EndY=-15.875 EndZ=0
    g1: LineSegment StartX=-320.258 StartY=-15.875 StartZ=0 EndX=-320.258 EndY=-31.75 EndZ=0
    g2: LineSegment StartX=-320.258 StartY=-31.75 StartZ=0 EndX=-421.858 EndY=-31.75 EndZ=0
    g3: LineSegment StartX=-421.858 StartY=-31.75 StartZ=0 EndX=-421.858 EndY=-15.875 EndZ=0
  constraints (11):
    c: Coincident(g0,g1)
    c: Coincident(g1,g2)
    c: Coincident(g2,g3)
    c: Coincident(g3,g0)
    c: Horizontal(g0)
    c: Horizontal(g2)
    c: Vertical(g1)
    c: Vertical(g3)
    c: Coincident(g0,g-3)
    c: DistanceY(g3,g3) = 15.875
    c: DistanceX(g2,g2) = 101.6
FEATURE [PartDesign::Pad] Pad013
  Direction = (1,-2e-16,3e-16)
  Length = 406.4
  Length2 = 10
  Midplane = true
  Placement = pos=(0,0,0) rot=(0.57735,0.57735,0.57735;2.0944rad)
  Profile = -> Sketch015
  ReferenceAxis = -> Sketch015 [N_Axis]
  Refine = true
  Type = 0
  expr: Length = <<Spreadsheet>>.width_x - 2 * <<Spreadsheet>>.base_rail_width
FEATURE [PartDesign::Body] Body008  label="LowerBraceFt"
  Group = -> [Clone2D008,Sketch015,Pad013]
  Origin = -> Origin008
  Tip = -> Pad013
FEATURE [Sketcher::SketchObject] Sketch016
  ExternalGeometry = -> [Clone2D009]
  FullyConstrained = true
  MapMode = 5
  Placement = pos=(0,0,0) rot=(0.57735,0.57735,0.57735;2.0944rad)
  Support = -> [YZ_Plane008]
  expr: Constraints[10] = <<Spreadsheet>>.base_stock_height
  expr: Constraints[9] = <<Spreadsheet>>.base_rail_width
  sketch-geometry (4):
    g0: LineSegment StartX=421.858 StartY=-15.875 StartZ=0 EndX=320.258 EndY=-15.875 EndZ=0
    g1: LineSegment StartX=320.258 StartY=-15.875 StartZ=0 EndX=320.258 EndY=-31.75 EndZ=0
    g2: LineSegment StartX=320.258 StartY=-31.75 StartZ=0 EndX=421.858 EndY=-31.75 EndZ=0
    g3: LineSegment StartX=421.858 StartY=-31.75 StartZ=0 EndX=421.858 EndY=-15.875 EndZ=0
  constraints (11):
    c: Coincident(g0,g1)
    c: Coincident(g1,g2)
    c: Coincident(g2,g3)
    c: Coincident(g3,g0)
    c: Horizontal(g0)
    c: Horizontal(g2)
    c: Vertical(g1)
    c: Vertical(g3)
    c: Coincident(g0,g-3)
    c: DistanceX(g0,g0) = 101.6
    c: DistanceY(g3,g3) = 15.875
FEATURE [PartDesign::Pad] Pad014
  Direction = (1,-2e-16,3e-16)
  Length = 406.4
  Length2 = 10
  Midplane = true
  Placement = pos=(0,0,0) rot=(0.57735,0.57735,0.57735;2.0944rad)
  Profile = -> Sketch016
  ReferenceAxis = -> Sketch016 [N_Axis]
  Refine = true
  Type = 0
  expr: Length = <<Spreadsheet>>.width_x - 2 * <<Spreadsheet>>.base_rail_width
FEATURE [PartDesign::Body] Body009  label="LowerBraceRr"
  Group = -> [Clone2D009,Sketch016,Pad014]
  Origin = -> Origin009
  Tip = -> Pad014
FEATURE [TechDraw::DrawSVGTemplate] Template
  Height = 210
  Orientation = 1
  Width = 297
FEATURE [TechDraw::DrawViewPart] View002  label="BottomShelfPerspective"
  CoarseView = false
  Direction = (0.577,-0.577,0.577)
  Focus = 100
  HardHidden = false
  IsoCount = 0
  IsoHidden = false
  IsoVisible = false
  LockPosition = false
  Perspective = false
  Rotation = 0
  Scale = 0.1
  ScaleType = 0
  SeamHidden = false
  SeamVisible = true
  SmoothHidden = false
  SmoothVisible = true
  Source = -> [Body]
  X = 164.956
  XDirection = (0.707,0.707,0)
  Y = 169.986
FEATURE [TechDraw::DrawViewPart] View003  label="LowerBracePerspective"
  CoarseView = false
  Direction = (0.577,-0.577,0.577)
  Focus = 100
  HardHidden = false
  IsoCount = 0
  IsoHidden = false
  IsoVisible = false
  LockPosition = false
  Perspective = false
  Rotation = 0
  Scale = 0.1
  ScaleType = 0
  SeamHidden = false
  SeamVisible = true
  SmoothHidden = false
  SmoothVisible = true
  Source = -> [Body009,Body008,Body002,Body001]
  X = 59.1543
  XDirection = (0.707,0.707,0)
  Y = 170.064
FEATURE [TechDraw::DrawProjGroupItem] ProjItem  label="BottomShelfTop"
  CoarseView = false
  Direction = (0,0,1)
  Focus = 100
  HardHidden = false
  IsoCount = 0
  IsoHidden = false
  IsoVisible = false
  LockPosition = true
  Perspective = false
  Rotation = 0
  RotationVector = (1,0,0)
  ScaleType = 2
  SeamHidden = false
  SeamVisible = true
  SmoothHidden = false
  SmoothVisible = true
  Source = -> [Body]
  Type = 0
  X = 0
  XDirection = (1,0,0)
  Y = 0
FEATURE [TechDraw::DrawProjGroupItem] ProjItem001  label="BottomShelfFront"
  CoarseView = false
  Direction = (0,-1,0)
  Focus = 100
  HardHidden = false
  IsoCount = 0
  IsoHidden = false
  IsoVisible = false
  LockPosition = false
  Perspective = false
  Rotation = 0
  RotationVector = (1,0,0)
  ScaleType = 2
  SeamHidden = false
  SeamVisible = true
  SmoothHidden = false
  SmoothVisible = true
  Source = -> [Body]
  Type = 5
  X = 0
  XDirection = (1,0,0)
  Y = 55.7544
FEATURE [TechDraw::DrawProjGroup] ProjGroup
  Anchor = -> ProjItem
  AutoDistribute = false
  LockPosition = false
  ProjectionType = 0
  Rotation = 0
  Scale = 0.1
  ScaleType = 0
  Source = -> [Body]
  Views = -> [ProjItem,ProjItem001]
  X = 162.409
  Y = 62.0952
  spacingX = 14.2875
  spacingY = 14.2875
FEATURE [TechDraw::DrawViewDimension] Dimension
  AngleOverride = false
  Arbitrary = false
  ArbitraryTolerances = false
  EqualTolerance = true
  ExtensionAngle = 0
  FormatSpec = %.2f
  FormatSpecOverTolerance = %+.2f
  FormatSpecUnderTolerance = %+.2f
  Inverted = false
  LineAngle = 0
  LockPosition = false
  MeasureType = 1
  OverTolerance = 0
  References2D = -> [ProjItem001]
  Rotation = 0
  Scale = 0.1
  ScaleType = 0
  TheoreticalExact = false
  Type = 2
  UnderTolerance = 0
  X = -40.3392
  Y = 1.98109
FEATURE [TechDraw::DrawProjGroupItem] ProjItem002  label="Front"
  CoarseView = false
  Direction = (0,0,1)
  Focus = 100
  HardHidden = false
  IsoCount = 0
  IsoHidden = false
  IsoVisible = false
  LockPosition = true
  Perspective = false
  Rotation = 0
  RotationVector = (1,0,0)
  ScaleType = 2
  SeamHidden = false
  SeamVisible = true
  SmoothHidden = false
  SmoothVisible = true
  Source = -> [Body001,Body002,Body009,Body008]
  Type = 0
  X = 0
  XDirection = (1,0,0)
  Y = 0
FEATURE [TechDraw::DrawProjGroupItem] ProjItem003  label="Bottom"
  CoarseView = false
  Direction = (0,-1,0)
  Focus = 100
  HardHidden = false
  IsoCount = 0
  IsoHidden = false
  IsoVisible = false
  LockPosition = false
  Perspective = false
  Rotation = 0
  RotationVector = (1,0,0)
  ScaleType = 2
  SeamHidden = false
  SeamVisible = true
  SmoothHidden = false
  SmoothVisible = true
  Source = -> [Body001,Body002,Body009,Body008]
  Type = 5
  X = 0
  XDirection = (1,0,0)
  Y = 53.3774
FEATURE [TechDraw::DrawProjGroup] ProjGroup001
  Anchor = -> ProjItem002
  AutoDistribute = false
  LockPosition = false
  ProjectionType = 0
  Rotation = 0
  Scale = 0.1
  ScaleType = 0
  Source = -> [Body001,Body002,Body009,Body008]
  Views = -> [ProjItem002,ProjItem003]
  X = 46.7725
  Y = 61.8901
  spacingX = 14.2875
  spacingY = 14.2875
FEATURE [TechDraw::DrawViewDimension] Dimension001
  AngleOverride = false
  Arbitrary = false
  ArbitraryTolerances = false
  EqualTolerance = true
  ExtensionAngle = 0
  FormatSpec = %.2f
  FormatSpecOverTolerance = %+.2f
  FormatSpecUnderTolerance = %+.2f
  Inverted = false
  LineAngle = 0
  LockPosition = false
  MeasureType = 1
  OverTolerance = 0
  References2D = -> [ProjItem003]
  Rotation = 0
  Scale = 0.1
  ScaleType = 0
  TheoreticalExact = false
  Type = 2
  UnderTolerance = 0
  X = -39.4744
  Y = 2.84594
FEATURE [TechDraw::DrawViewDimension] Dimension002
  AngleOverride = false
  Arbitrary = false
  ArbitraryTolerances = false
  EqualTolerance = true
  ExtensionAngle = 0
  FormatSpec = %.2f
  FormatSpecOverTolerance = %+.2f
  FormatSpecUnderTolerance = %+.2f
  Inverted = false
  LineAngle = 0
  LockPosition = false
  MeasureType = 1
  OverTolerance = 0
  References2D = -> [ProjItem002]
  Rotation = 0
  Scale = 0.1
  ScaleType = 0
  TheoreticalExact = false
  Type = 2
  UnderTolerance = 0
  X = 23.9226
  Y = 1.22435
FEATURE [TechDraw::DrawViewDimension] Dimension003
  AngleOverride = false
  Arbitrary = false
  ArbitraryTolerances = false
  EqualTolerance = true
  ExtensionAngle = 0
  FormatSpec = %.2f
  FormatSpecOverTolerance = %+.2f
  FormatSpecUnderTolerance = %+.2f
  Inverted = false
  LineAngle = 0
  LockPosition = false
  MeasureType = 1
  OverTolerance = 0
  References2D = -> [ProjItem002]
  Rotation = 0
  Scale = 0.1
  ScaleType = 0
  TheoreticalExact = false
  Type = 1
  UnderTolerance = 0
  X = 12.9854
  Y = 29.2992
FEATURE [TechDraw::DrawViewDimension] Dimension004
  AngleOverride = false
  Arbitrary = false
  ArbitraryTolerances = false
  EqualTolerance = true
  ExtensionAngle = 0
  FormatSpec = %.2f
  FormatSpecOverTolerance = %+.2f
  FormatSpecUnderTolerance = %+.2f
  Inverted = false
  LineAngle = 0
  LockPosition = false
  MeasureType = 1
  OverTolerance = 0
  References2D = -> [ProjItem002]
  Rotation = 0
  Scale = 0.1
  ScaleType = 0
  TheoreticalExact = false
  Type = 2
  UnderTolerance = 0
  X = -14.1953
  Y = -18.3487
FEATURE [TechDraw::DrawViewDimension] Dimension006
  AngleOverride = false
  Arbitrary = false
  ArbitraryTolerances = false
  EqualTolerance = true
  ExtensionAngle = 0
  FormatSpec = %.2f
  FormatSpecOverTolerance = %+.2f
  FormatSpecUnderTolerance = %+.2f
  Inverted = false
  LineAngle = 0
  LockPosition = false
  MeasureType = 1
  OverTolerance = 0
  References2D = -> [ProjItem]
  Rotation = 0
  Scale = 0.1
  ScaleType = 0
  TheoreticalExact = false
  Type = 2
  UnderTolerance = 0
  X = -25.5294
  Y = 3.6787
FEATURE [TechDraw::DrawViewDimension] Dimension007
  AngleOverride = false
  Arbitrary = false
  ArbitraryTolerances = false
  EqualTolerance = true
  ExtensionAngle = 0
  FormatSpec = %.2f
  FormatSpecOverTolerance = %+.2f
  FormatSpecUnderTolerance = %+.2f
  Inverted = false
  LineAngle = 0
  LockPosition = false
  MeasureType = 1
  OverTolerance = 0
  References2D = -> [ProjItem]
  Rotation = 0
  Scale = 0.1
  ScaleType = 0
  TheoreticalExact = false
  Type = 1
  UnderTolerance = 0
  X = 0.235741
  Y = 39.7587
FEATURE [TechDraw::DrawViewDimension] Dimension008
  AngleOverride = false
  Arbitrary = false
  ArbitraryTolerances = false
  EqualTolerance = true
  ExtensionAngle = 0
  FormatSpec = %.2f
  FormatSpecOverTolerance = %+.2f
  FormatSpecUnderTolerance = %+.2f
  Inverted = false
  LineAngle = 0
  LockPosition = false
  MeasureType = 1
  OverTolerance = 0
  References2D = -> [ProjItem002]
  Rotation = 0
  Scale = 0.1
  ScaleType = 0
  TheoreticalExact = false
  Type = 1
  UnderTolerance = 0
  X = 0.471481
  Y = 39.7121
FEATURE [TechDraw::DrawViewPart] View  label="TopShelfPerspective"
  CoarseView = false
  Direction = (0.577,-0.577,0.577)
  Focus = 100
  HardHidden = false
  IsoCount = 0
  IsoHidden = false
  IsoVisible = false
  LockPosition = false
  Perspective = false
  Rotation = 0
  Scale = 0.1
  ScaleType = 0
  SeamHidden = false
  SeamVisible = true
  SmoothHidden = false
  SmoothVisible = true
  Source = -> [Body007]
  X = 257.019
  XDirection = (0.707,0.707,0)
  Y = 137.121
FEATURE [TechDraw::DrawProjGroupItem] ProjItem004  label="TopShelfTop"
  CoarseView = false
  Direction = (0,0,1)
  Focus = 100
  HardHidden = false
  IsoCount = 0
  IsoHidden = false
  IsoVisible = false
  LockPosition = true
  Perspective = false
  Rotation = 0
  RotationVector = (1,0,0)
  ScaleType = 2
  SeamHidden = false
  SeamVisible = true
  SmoothHidden = false
  SmoothVisible = true
  Source = -> [Body007]
  Type = 0
  X = 0
  XDirection = (1,0,0)
  Y = 0
FEATURE [TechDraw::DrawProjGroupItem] ProjItem005  label="TopShelfFront"
  CoarseView = false
  Direction = (0,-1,0)
  Focus = 100
  HardHidden = false
  IsoCount = 0
  IsoHidden = false
  IsoVisible = false
  LockPosition = false
  Perspective = false
  Rotation = 0
  RotationVector = (1,0,0)
  ScaleType = 2
  SeamHidden = false
  SeamVisible = true
  SmoothHidden = false
  SmoothVisible = true
  Source = -> [Body007]
  Type = 5
  X = 0
  XDirection = (1,0,0)
  Y = 34.0947
FEATURE [TechDraw::DrawProjGroup] ProjGroup002
  Anchor = -> ProjItem004
  AutoDistribute = false
  LockPosition = false
  ProjectionType = 0
  Rotation = 0
  Scale = 0.1
  ScaleType = 0
  Source = -> [Body007]
  Views = -> [ProjItem004,ProjItem005]
  X = 255.495
  Y = 61.9601
  spacingX = 14.2875
  spacingY = 14.2875
FEATURE [TechDraw::DrawViewDimension] Dimension009
  AngleOverride = false
  Arbitrary = false
  ArbitraryTolerances = false
  EqualTolerance = true
  ExtensionAngle = 0
  FormatSpec = %.2f
  FormatSpecOverTolerance = %+.2f
  FormatSpecUnderTolerance = %+.2f
  Inverted = false
  LineAngle = 0
  LockPosition = false
  MeasureType = 1
  OverTolerance = 0
  References2D = -> [ProjItem005]
  Rotation = 0
  Scale = 0.1
  ScaleType = 0
  TheoreticalExact = false
  Type = 2
  UnderTolerance = 0
  X = -38.5749
  Y = 2.08487
FEATURE [TechDraw::DrawViewDimension] Dimension010
  AngleOverride = false
  Arbitrary = false
  ArbitraryTolerances = false
  EqualTolerance = true
  ExtensionAngle = 0
  FormatSpec = %.2f
  FormatSpecOverTolerance = %+.2f
  FormatSpecUnderTolerance = %+.2f
  Inverted = false
  LineAngle = 0
  LockPosition = false
  MeasureType = 1
  OverTolerance = 0
  References2D = -> [ProjItem004]
  Rotation = 0
  Scale = 0.1
  ScaleType = 0
  TheoreticalExact = false
  Type = 1
  UnderTolerance = 0
  X = -1.19556
  Y = 11.3889
FEATURE [TechDraw::DrawViewDimension] Dimension011
  AngleOverride = false
  Arbitrary = false
  ArbitraryTolerances = false
  EqualTolerance = true
  ExtensionAngle = 0
  FormatSpec = %.2f
  FormatSpecOverTolerance = %+.2f
  FormatSpecUnderTolerance = %+.2f
  Inverted = false
  LineAngle = 0
  LockPosition = false
  MeasureType = 1
  OverTolerance = 0
  References2D = -> [ProjItem004]
  Rotation = 0
  Scale = 0.1
  ScaleType = 0
  TheoreticalExact = false
  Type = 2
  UnderTolerance = 0
  X = -24.9505
  Y = 2.20111
FEATURE [TechDraw::DrawPage] Page  label="BaseAndShelf"
  KeepUpdated = true
  NextBalloonIndex = 1
  ProjectionType = 0
  Scale = 0.1
  Template = -> Template
  Views = -> [View002,View003,ProjGroup,Dimension,ProjGroup001,Dimension001,Dimension002,Dimension003,Dimension004,Dimension006,Dimension007,Dimension008,View,ProjGroup002,Dimension009,Dimension010,Dimension011]
  expr: Scale = 1 / 10
FEATURE [TechDraw::DrawSVGTemplate] Template001
  EditableTexts = Designed_by_Name=Jason Stiles; FC-Date=23 MAR 2023; FC-SC=1/10; FC-SH=1; FC-Title=Clamp Stand
  Height = 210
  Orientation = 1
  Width = 297
FEATURE [TechDraw::DrawViewPart] View004  label="Perspective"
  CoarseView = false
  Direction = (0.577,-0.577,0.577)
  Focus = 100
  HardHidden = false
  IsoCount = 0
  IsoHidden = false
  IsoVisible = false
  LockPosition = false
  Perspective = false
  Rotation = 0
  Scale = 0.1
  ScaleType = 0
  SeamHidden = false
  SeamVisible = true
  SmoothHidden = false
  SmoothVisible = true
  Source = -> [Body005,Body004,Body003,Body002,Body001,Body,Body006,Body007,Body008,Body009]
  X = 80.3531
  XDirection = (0.707,0.707,0)
  Y = 103.924
FEATURE [TechDraw::DrawPage] Page001  label="Title"
  KeepUpdated = true
  NextBalloonIndex = 1
  ProjectionType = 0
  Scale = 0.1
  Template = -> Template001
  Views = -> [View004]
  expr: Scale = 1 / 10
FEATURE [TechDraw::DrawSVGTemplate] Template002
  Height = 297
  Orientation = 0
  Width = 210
FEATURE [TechDraw::DrawViewPart] View006  label="RiserSide"
  CoarseView = false
  Direction = (1,0,0)
  Focus = 100
  HardHidden = false
  IsoCount = 0
  IsoHidden = false
  IsoVisible = false
  LockPosition = false
  Perspective = false
  Rotation = 0
  Scale = 0.1
  ScaleType = 0
  SeamHidden = false
  SeamVisible = true
  SmoothHidden = false
  SmoothVisible = true
  Source = -> [Body004]
  X = 56.6872
  XDirection = (0,1,0)
  Y = 201.521
FEATURE [TechDraw::DrawViewDimension] Dimension012
  AngleOverride = false
  Arbitrary = false
  ArbitraryTolerances = false
  EqualTolerance = true
  ExtensionAngle = 0
  FormatSpec = %.2f
  FormatSpecOverTolerance = %+.2f
  FormatSpecUnderTolerance = %+.2f
  Inverted = false
  LineAngle = 0
  LockPosition = false
  MeasureType = 1
  OverTolerance = 0
  References2D = -> [View006]
  Rotation = 0
  Scale = 0.1
  ScaleType = 0
  TheoreticalExact = false
  Type = 0
  UnderTolerance = 0
  X = 13.5433
  Y = 0.879284
FEATURE [TechDraw::DrawViewDimension] Dimension013
  AngleOverride = false
  Arbitrary = false
  ArbitraryTolerances = false
  EqualTolerance = true
  ExtensionAngle = 0
  FormatSpec = %.2f
  FormatSpecOverTolerance = %+.2f
  FormatSpecUnderTolerance = %+.2f
  Inverted = false
  LineAngle = 0
  LockPosition = false
  MeasureType = 1
  OverTolerance = 0
  References2D = -> [View006]
  Rotation = 0
  Scale = 0.1
  ScaleType = 0
  TheoreticalExact = false
  Type = 6
  UnderTolerance = 0
  X = -8.10358
  Y = 67.144
FEATURE [TechDraw::DrawViewDimension] Dimension014
  AngleOverride = false
  Arbitrary = false
  ArbitraryTolerances = false
  EqualTolerance = true
  ExtensionAngle = 0
  FormatSpec = %.2f
  FormatSpecOverTolerance = %+.2f
  FormatSpecUnderTolerance = %+.2f
  Inverted = false
  LineAngle = 0
  LockPosition = false
  MeasureType = 1
  OverTolerance = 0
  References2D = -> [View006]
  Rotation = 0
  Scale = 0.1
  ScaleType = 0
  TheoreticalExact = false
  Type = 0
  UnderTolerance = 0
  X = 22.4801
  Y = -10.8515
FEATURE [TechDraw::DrawViewDimension] Dimension015
  AngleOverride = false
  Arbitrary = false
  ArbitraryTolerances = false
  EqualTolerance = true
  ExtensionAngle = 0
  FormatSpec = %.2f
  FormatSpecOverTolerance = %+.2f
  FormatSpecUnderTolerance = %+.2f
  Inverted = false
  LineAngle = 0
  LockPosition = false
  MeasureType = 1
  OverTolerance = 0
  References2D = -> [View006]
  Rotation = 0
  Scale = 0.1
  ScaleType = 0
  TheoreticalExact = false
  Type = 0
  UnderTolerance = 0
  X = 2.37261
  Y = 77.8534
FEATURE [TechDraw::DrawViewDimension] Dimension016
  AngleOverride = false
  Arbitrary = false
  ArbitraryTolerances = false
  EqualTolerance = true
  ExtensionAngle = 0
  FormatSpec = %.2f
  FormatSpecOverTolerance = %+.2f
  FormatSpecUnderTolerance = %+.2f
  Inverted = false
  LineAngle = 0
  LockPosition = false
  MeasureType = 1
  OverTolerance = 0
  References2D = -> [View006]
  Rotation = 0
  Scale = 0.1
  ScaleType = 0
  TheoreticalExact = false
  Type = 0
  UnderTolerance = 0
  X = -24.3986
  Y = -72.6576
FEATURE [TechDraw::DrawViewDimension] Dimension017
  AngleOverride = false
  Arbitrary = false
  ArbitraryTolerances = false
  EqualTolerance = true
  ExtensionAngle = 0
  FormatSpec = %.2f
  FormatSpecOverTolerance = %+.2f
  FormatSpecUnderTolerance = %+.2f
  Inverted = false
  LineAngle = 0
  LockPosition = false
  MeasureType = 1
  OverTolerance = 0
  References2D = -> [View006]
  Rotation = 0
  Scale = 0.1
  ScaleType = 0
  TheoreticalExact = false
  Type = 0
  UnderTolerance = 0
  X = -22.1729
  Y = -37.1768
FEATURE [TechDraw::DrawViewDimension] Dimension018
  AngleOverride = false
  Arbitrary = false
  ArbitraryTolerances = false
  EqualTolerance = true
  ExtensionAngle = 0
  FormatSpec = %.2f
  FormatSpecOverTolerance = %+.2f
  FormatSpecUnderTolerance = %+.2f
  Inverted = false
  LineAngle = 0
  LockPosition = false
  MeasureType = 1
  OverTolerance = 0
  References2D = -> [View006]
  Rotation = 0
  Scale = 0.1
  ScaleType = 0
  TheoreticalExact = false
  Type = 0
  UnderTolerance = 0
  X = -14.7009
  Y = 4.35225
FEATURE [TechDraw::DrawViewDimension] Dimension019
  AngleOverride = false
  Arbitrary = false
  ArbitraryTolerances = false
  EqualTolerance = true
  ExtensionAngle = 0
  FormatSpec = %.2f
  FormatSpecOverTolerance = %+.2f
  FormatSpecUnderTolerance = %+.2f
  Inverted = false
  LineAngle = 0
  LockPosition = false
  MeasureType = 1
  OverTolerance = 0
  References2D = -> [View006]
  Rotation = 0
  Scale = 0.1
  ScaleType = 0
  TheoreticalExact = false
  Type = 0
  UnderTolerance = 0
  X = -7.26207
  Y = 45.614
FEATURE [TechDraw::DrawViewPart] View008  label="RiserFront"
  CoarseView = false
  Direction = (0,-1,0)
  Focus = 100
  HardHidden = false
  IsoCount = 0
  IsoHidden = false
  IsoVisible = false
  LockPosition = false
  Perspective = false
  Rotation = 0
  Scale = 0.1
  ScaleType = 0
  SeamHidden = false
  SeamVisible = true
  SmoothHidden = false
  SmoothVisible = true
  Source = -> [Body003,Body004]
  X = 143.203
  XDirection = (1,0,0)
  Y = 200.826
FEATURE [TechDraw::DrawViewDimension] Dimension020
  AngleOverride = false
  Arbitrary = false
  ArbitraryTolerances = false
  EqualTolerance = true
  ExtensionAngle = 0
  FormatSpec = %.2f
  FormatSpecOverTolerance = %+.2f
  FormatSpecUnderTolerance = %+.2f
  Inverted = false
  LineAngle = 0
  LockPosition = false
  MeasureType = 1
  OverTolerance = 0
  References2D = -> [View008]
  Rotation = 0
  Scale = 0.1
  ScaleType = 0
  TheoreticalExact = false
  Type = 0
  UnderTolerance = 0
  X = -0.463062
  Y = -12.3367
FEATURE [TechDraw::DrawViewDimension] Dimension021
  AngleOverride = false
  Arbitrary = false
  ArbitraryTolerances = false
  EqualTolerance = true
  ExtensionAngle = 0
  FormatSpec = %.2f
  FormatSpecOverTolerance = %+.2f
  FormatSpecUnderTolerance = %+.2f
  Inverted = false
  LineAngle = 0
  LockPosition = false
  MeasureType = 1
  OverTolerance = 0
  References2D = -> [View006]
  Rotation = 0
  Scale = 0.1
  ScaleType = 0
  TheoreticalExact = false
  Type = 0
  UnderTolerance = 0
  X = 19.4793
  Y = 21.5922
FEATURE [TechDraw::DrawViewDimension] Dimension022
  AngleOverride = false
  Arbitrary = false
  ArbitraryTolerances = false
  EqualTolerance = true
  ExtensionAngle = 0
  FormatSpec = %.2f
  FormatSpecOverTolerance = %+.2f
  FormatSpecUnderTolerance = %+.2f
  Inverted = false
  LineAngle = 0
  LockPosition = false
  MeasureType = 1
  OverTolerance = 0
  References2D = -> [View006]
  Rotation = 0
  Scale = 0.1
  ScaleType = 0
  TheoreticalExact = false
  Type = 0
  UnderTolerance = 0
  X = 5.41898
  Y = 35.3778
FEATURE [TechDraw::DrawPage] Page002  label="Risers and Stretchers"
  KeepUpdated = true
  NextBalloonIndex = 1
  ProjectionType = 0
  Scale = 0.1
  Template = -> Template002
  Views = -> [View006,Dimension012,Dimension013,Dimension014,Dimension015,Dimension016,Dimension017,Dimension018,Dimension019,View008,Dimension020,Dimension021,Dimension022]
  expr: Scale = 1 / 10
FEATURE [App::LinkGroup] LinkGroup  label="Drawings"
  ElementList = -> [Page001,Page,Page002]
  LinkMode = 0
